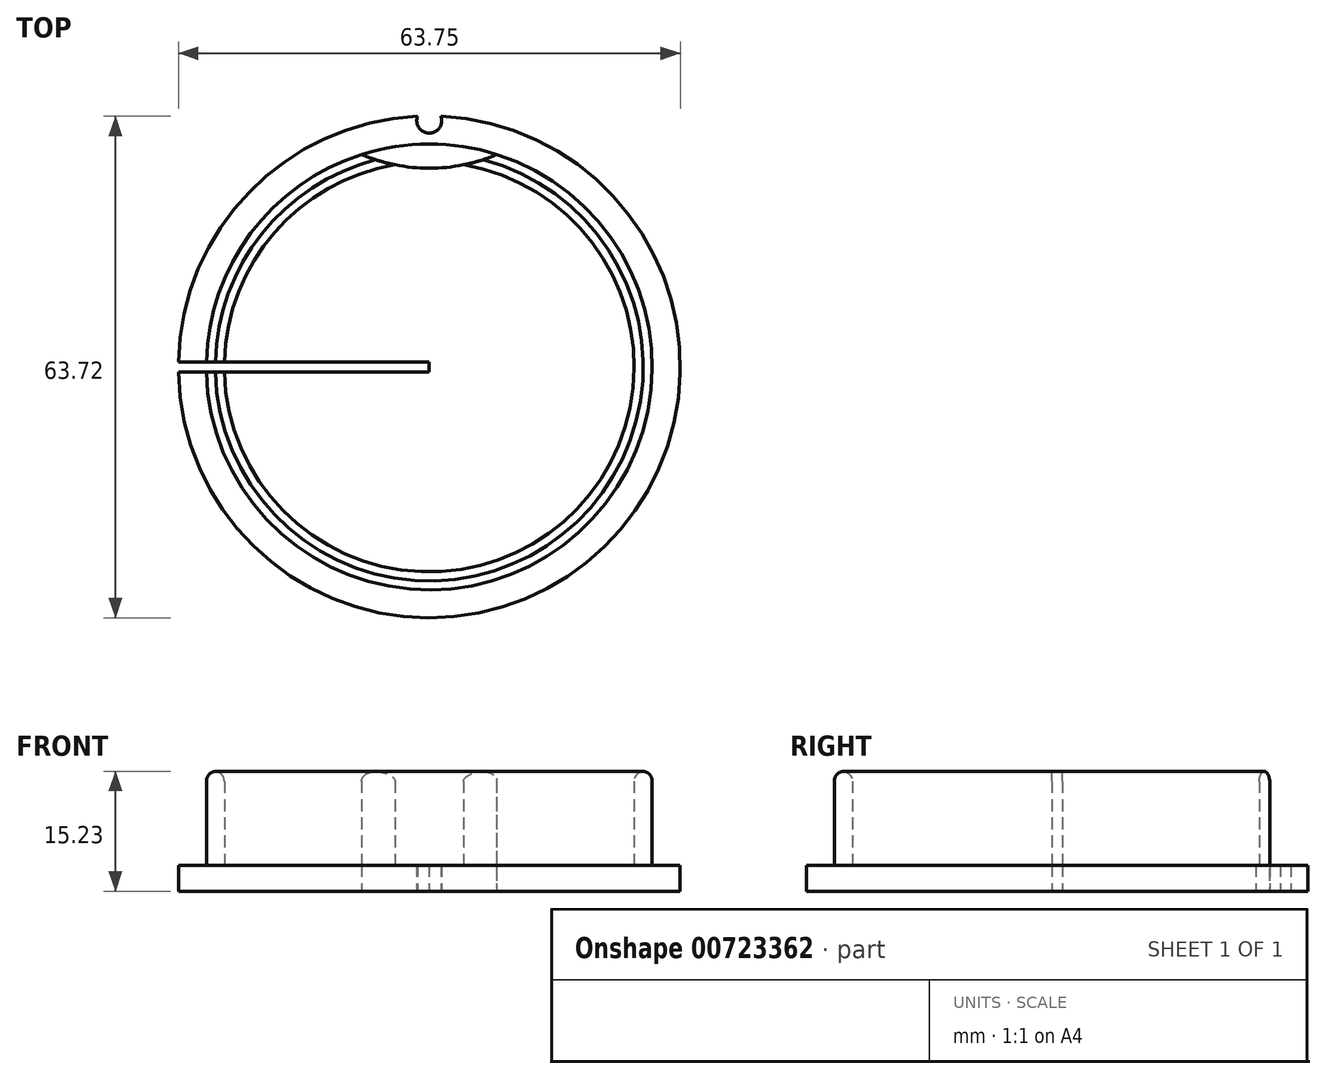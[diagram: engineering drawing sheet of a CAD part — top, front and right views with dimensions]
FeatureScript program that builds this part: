
annotation { "Feature Type Name" : "Feature", "Feature Type Description" : "" }
export const myFeature = defineFeature(function(context is Context, id is Id, definition is map)
    precondition{}
    {
        {
            var Q0;
            Q0=qCreatedBy(makeId("Top.planeOp"),FACE);
            var sketch = newSketch(context, id + "F0", { "sketchPlane" : qUnion([Q0])});
            skCircle(sketch, "E0", {"center": v(0, 0) * mm, "radius": 31.88 * mm});
            skCircle(sketch, "E1", {"center": v(0, 0) * mm, "radius": 28.32 * mm});
            skCircle(sketch, "E2", {"center": v(0, 0) * mm, "radius": 26.04 * mm});
            skSolve(sketch);
        }
        {
            var Q0;
            Q0=qCreatedBy(makeId("Top.planeOp"),FACE);
            var sketch = newSketch(context, id + "F1", { "sketchPlane" : qUnion([Q0])});
            skCircle(sketch, "E3", {"center": v(0, 0) * mm, "radius": 31.88 * mm});
            skSolve(sketch);
        }
        {
            var Q0;
            Q0 = qSketchRegion(id + "F1", true);
            extrude(context, id + "F2", {"entities" : qUnion([Q0]), "depth" : 3.3 * mm, "offsetDistance" : 25.4 * mm});
        }
        {
            var Q0;
            Q0=makeQuery(id+"F0.imprint","IMPRINT",FACE,{"disambiguationData":[TD([[makeQuery(id+"F0.imprint","IMPRINT",EDGE,{"derivedFrom":sQuery(id+"F0.wireOp",EDGE,"E1")}),1.0]])]});
            var Q1;
            Q1=sQuery(id+"F0.wireOp",EDGE,"E2");
            var Q2;
            Q2=sQuery(id+"F0.wireOp",EDGE,"E1");
            extrude(context, id + "F3", {"entities" : qUnion([Q0]), "operationType" : NewBodyOperationType.ADD, "surfaceEntities" : qUnion([Q1, Q2]), "depth" : 15.24 * mm, "offsetDistance" : 25.4 * mm});
        }
        {
            var Q0;
            Q0=qCreatedBy(makeId("Top.planeOp"),FACE);
            var sketch = newSketch(context, id + "F4", { "sketchPlane" : qUnion([Q0])});
            skLineSegment(sketch, "E4", {"start": v(0, 0) * mm, "end": v(0, -0.64) * mm});
            skLineSegment(sketch, "E5", {"start": v(0, 0) * mm, "end": v(0, 0.64) * mm});
            skLineSegment(sketch, "E6", {"start": v(0, -0.64) * mm, "end": v(-31.9, -0.64) * mm});
            skLineSegment(sketch, "E7", {"start": v(0, 0.64) * mm, "end": v(-31.95, 0.64) * mm});
            skLineSegment(sketch, "E8", {"start": v(-31.95, 0.64) * mm, "end": v(-31.9, -0.64) * mm});
            skSolve(sketch);
        }
        {
            var Q0;
            Q0=makeQuery(id+"F4.imprint","IMPRINT",FACE,{"disambiguationData":[TD([[makeQuery(id+"F4.imprint","IMPRINT",EDGE,{"derivedFrom":sQuery(id+"F4.wireOp",EDGE,"E4")}),-1.0]])]});
            extrude(context, id + "F5", {"entities" : qUnion([Q0]), "operationType" : NewBodyOperationType.REMOVE, "depth" : 25.4 * mm, "offsetDistance" : 25.4 * mm});
        }
        {
            var Q0;
            Q0=makeQuery(id+"F1.imprint","IMPRINT",FACE,{"disambiguationData":[TD([[makeQuery(id+"F1.imprint","IMPRINT",EDGE,{"derivedFrom":sQuery(id+"F1.wireOp",EDGE,"E3")}),1.0]])]});
            var sketch = newSketch(context, id + "F6", { "sketchPlane" : qUnion([Q0])});
            skCircle(sketch, "E9", {"center": v(0, 31.28) * mm, "radius": 1.59 * mm});
            skSolve(sketch);
        }
        {
            var Q0;
            {var subQ0=sQuery(id+"F6.wireOp",EDGE,"E9");var subQ1=makeQuery(id+"F1.imprint","IMPRINT",EDGE,{"derivedFrom":sQuery(id+"F1.wireOp",EDGE,"E3")});var subQ2=makeQuery(id+"F6.imprint","INTERSECT",VERTEX,{"disambiguationData":[OD(0.0)],"derivedFrom":[subQ1,subQ0]});Q0=makeQuery(id+"F6.imprint","IMPRINT",FACE,{"disambiguationData":[TD([[makeQuery(id+"F6.imprint","IMPRINT",EDGE,{"disambiguationData":[TD([[subQ2,-1.0]])],"derivedFrom":subQ0}),1.0]])]});}
            var Q1;
            Q1=sQuery(id+"F6.wireOp",EDGE,"E9");
            extrude(context, id + "F7", {"entities" : qUnion([Q0]), "operationType" : NewBodyOperationType.REMOVE, "surfaceEntities" : qUnion([Q1]), "depth" : 25.4 * mm, "offsetDistance" : 25.4 * mm});
        }
        {
            var Q0;
            Q0=qCreatedBy(makeId("Top.planeOp"),FACE);
            var sketch = newSketch(context, id + "F8", { "sketchPlane" : qUnion([Q0])});
            skArc(sketch, "E10", {"start": v(-8.53, 26.96) * mm, "mid": v(0, 25.24) * mm, "end": v(8.52, 26.96) * mm});
            skLineSegment(sketch, "E11", {"start": v(0, 0) * mm, "end": v(0, 25.27) * mm});
            skArc(sketch, "E12", {"start": v(8.56, 27) * mm, "mid": v(-0.02, 28.32) * mm, "end": v(-8.6, 26.99) * mm});
            skLineSegment(sketch, "E13", {"start": v(-8.53, 26.96) * mm, "end": v(-8.6, 26.99) * mm});
            skLineSegment(sketch, "E14", {"start": v(8.52, 26.96) * mm, "end": v(8.56, 27) * mm});
            skSolve(sketch);
        }
        {
            var Q0;
            Q0=makeQuery(id+"F8.imprint","IMPRINT",FACE,{"disambiguationData":[TD([[makeQuery(id+"F8.imprint","IMPRINT",EDGE,{"derivedFrom":sQuery(id+"F8.wireOp",EDGE,"E12")}),1.0]])]});
            extrude(context, id + "F9", {"entities" : qUnion([Q0]), "operationType" : NewBodyOperationType.REMOVE, "depth" : 25.4 * mm, "offsetDistance" : 25.4 * mm});
        }
        {
            var Q0;
            {var subQ0=sQuery(id+"F0.wireOp",EDGE,"E1");Q0=makeQuery(id+"F9.boolean.opBoolean","SPLIT",EDGE,{"disambiguationData":[TD([makeQuery(id+"F5.boolean.opBoolean","COPY",FACE,{"derivedFrom":makeQuery(id+"F5.opExtrude","SWEPT_FACE",FACE,{"disambiguationData":[OSD([sQuery(id+"F4.wireOp",EDGE,"E6")])]})})])],"derivedFrom":makeQuery(id+"F3.opExtrude","CAP_EDGE",EDGE,{"disambiguationData":[OSD([subQ0])],"isStart":false})});}
            var Q1;
            {var subQ0=sQuery(id+"F0.wireOp",EDGE,"E1");Q1=makeQuery(id+"F9.boolean.opBoolean","SPLIT",EDGE,{"disambiguationData":[TD([makeQuery(id+"F5.boolean.opBoolean","COPY",FACE,{"derivedFrom":makeQuery(id+"F5.opExtrude","SWEPT_FACE",FACE,{"disambiguationData":[OSD([sQuery(id+"F4.wireOp",EDGE,"E7")])]})})])],"derivedFrom":makeQuery(id+"F3.opExtrude","CAP_EDGE",EDGE,{"disambiguationData":[OSD([subQ0])],"isStart":false})});}
            var Q2;
            {var subQ0=sQuery(id+"F0.wireOp",EDGE,"E2");Q2=makeQuery(id+"F9.boolean.opBoolean","SPLIT",EDGE,{"disambiguationData":[TD([makeQuery(id+"F5.boolean.opBoolean","COPY",FACE,{"derivedFrom":makeQuery(id+"F5.opExtrude","SWEPT_FACE",FACE,{"disambiguationData":[OSD([sQuery(id+"F4.wireOp",EDGE,"E7")])]})})])],"derivedFrom":makeQuery(id+"F3.opExtrude","CAP_EDGE",EDGE,{"disambiguationData":[OSD([subQ0])],"isStart":false})});}
            var Q3;
            {var subQ0=sQuery(id+"F0.wireOp",EDGE,"E2");Q3=makeQuery(id+"F9.boolean.opBoolean","SPLIT",EDGE,{"disambiguationData":[TD([makeQuery(id+"F5.boolean.opBoolean","COPY",FACE,{"derivedFrom":makeQuery(id+"F5.opExtrude","SWEPT_FACE",FACE,{"disambiguationData":[OSD([sQuery(id+"F4.wireOp",EDGE,"E6")])]})})])],"derivedFrom":makeQuery(id+"F3.opExtrude","CAP_EDGE",EDGE,{"disambiguationData":[OSD([subQ0])],"isStart":false})});}
            fillet(context, id + "F10", {"entities" : qUnion([Q0, Q1, Q2, Q3]), "radius" : 1.27 * mm, "tangentPropagation" : true, "allowEdgeOverflow" : false});
        }
    });
